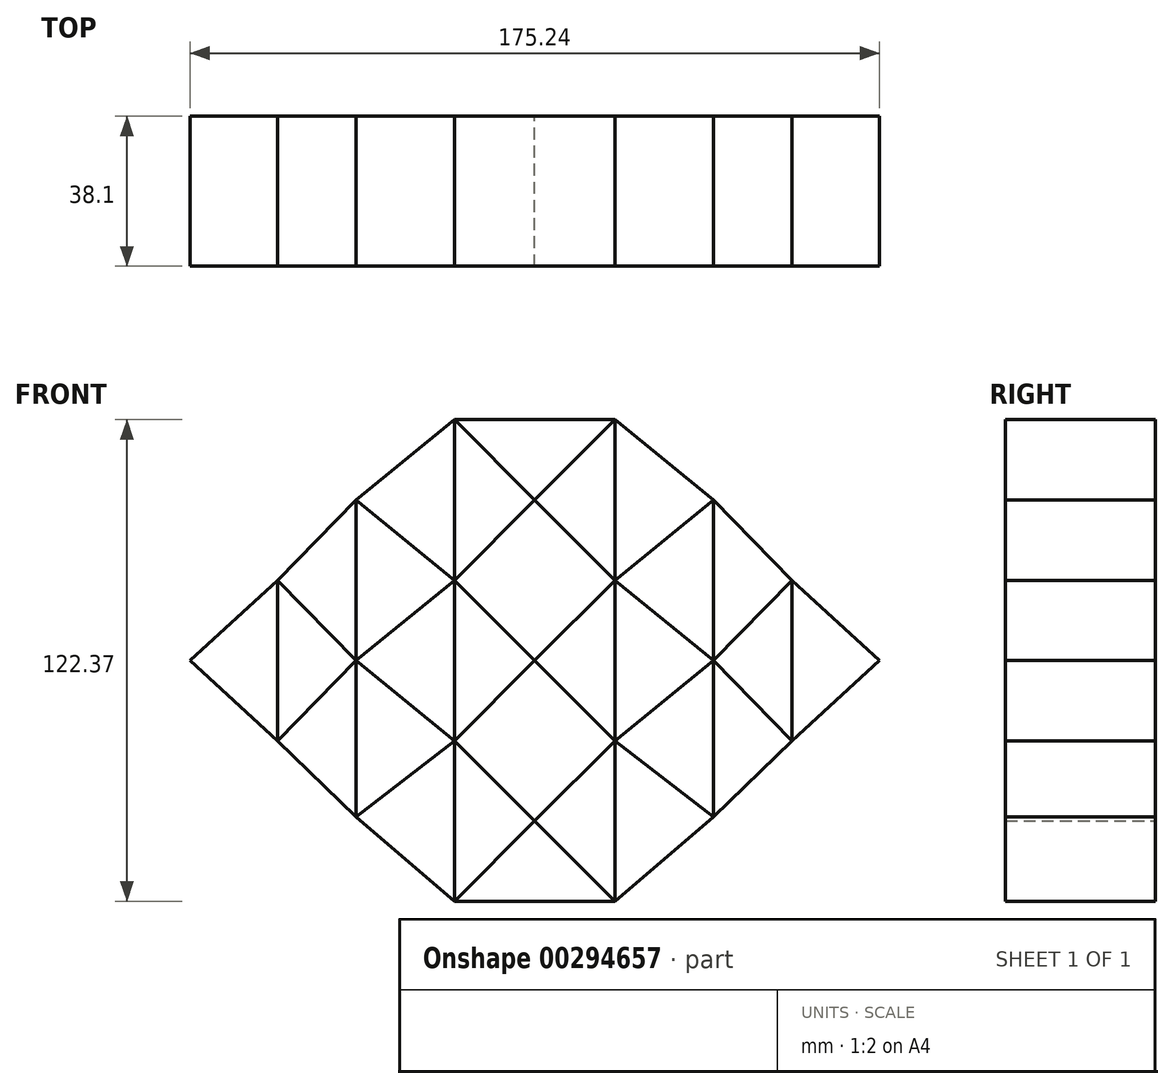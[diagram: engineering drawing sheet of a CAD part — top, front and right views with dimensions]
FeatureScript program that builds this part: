
annotation { "Feature Type Name" : "Feature", "Feature Type Description" : "" }
export const myFeature = defineFeature(function(context is Context, id is Id, definition is map)
    precondition{}
    {
        {
            var Q0;
            Q0=qCreatedBy(makeId("Front.planeOp"),FACE);
            var sketch = newSketch(context, id + "F0", { "sketchPlane" : qUnion([Q0])});
            skLineSegment(sketch, "E0", {"start": v(-20.4, 76.52) * mm, "end": v(16.8, 39.33) * mm});
            skLineSegment(sketch, "E1.MirrorCS", {"start": v(20.4, 76.52) * mm, "end": v(0, 56.12) * mm});
            skLineSegment(sketch, "E2.MirrorCS", {"start": v(-20.4, 35.73) * mm, "end": v(0, 56.12) * mm});
            skLineSegment(sketch, "E3.MirrorCS", {"start": v(16.8, 39.33) * mm, "end": v(-3.6, 59.72) * mm});
            skLineSegment(sketch, "E4.MirrorCS", {"start": v(-20.4, 35.73) * mm, "end": v(15.33, 0) * mm});
            skLineSegment(sketch, "E5.MirrorCS", {"start": v(20.4, 35.73) * mm, "end": v(0, 15.33) * mm});
            skLineSegment(sketch, "E6.MirrorCS", {"start": v(-20.4, -5.06) * mm, "end": v(0, 15.33) * mm});
            skLineSegment(sketch, "E7.MirrorCS", {"start": v(20.4, -5.06) * mm, "end": v(0, 15.33) * mm});
            skPoint(sketch, "E8.end.orphan", {"position": v(0, 0) * mm});
            skPoint(sketch, "E8.start.orphan", {"position": v(-20.4, 35.73) * mm});
            skPoint(sketch, "E9.start.orphan", {"position": v(16.8, 39.33) * mm});
            skLineSegment(sketch, "E10.MirrorCS", {"start": v(-20.4, -5.06) * mm, "end": v(0, -25.46) * mm});
            skLineSegment(sketch, "E11.MirrorCS", {"start": v(20.4, -5.06) * mm, "end": v(0, -25.46) * mm});
            skLineSegment(sketch, "E12.MirrorCS", {"start": v(-20.4, -45.85) * mm, "end": v(0, -25.46) * mm});
            skLineSegment(sketch, "E13.MirrorCS", {"start": v(20.4, -45.85) * mm, "end": v(0, -25.46) * mm});
            skPoint(sketch, "E14.orphan", {"position": v(0, 76.52) * mm});
            skLineSegment(sketch, "E15", {"start": v(-20.4, 76.52) * mm, "end": v(-20.4, -45.85) * mm});
            skLineSegment(sketch, "E16", {"start": v(20.4, -45.85) * mm, "end": v(20.4, 76.52) * mm});
            skLineSegment(sketch, "E17", {"start": v(20.4, 76.52) * mm, "end": v(-20.4, 76.52) * mm});
            skLineSegment(sketch, "E18", {"start": v(-20.4, -45.85) * mm, "end": v(20.4, -45.85) * mm});
            skLineSegment(sketch, "E19", {"start": v(16.8, 39.33) * mm, "end": v(20.4, 35.73) * mm});
            skPoint(sketch, "E20.start.orphan", {"position": v(20.4, 16.97) * mm});
            skPoint(sketch, "E21.endSnap0", {"position": v(20.4, 15.33) * mm});
            skLineSegment(sketch, "E22", {"start": v(45.38, 56.12) * mm, "end": v(20.4, 76.52) * mm});
            skLineSegment(sketch, "E23", {"start": v(45.38, 56.12) * mm, "end": v(20.4, 35.73) * mm});
            skLineSegment(sketch, "E24", {"start": v(20.4, 35.73) * mm, "end": v(45.38, 15.33) * mm});
            skLineSegment(sketch, "E25", {"start": v(45.38, 15.33) * mm, "end": v(20.4, -5.06) * mm});
            skLineSegment(sketch, "E26", {"start": v(20.4, -5.06) * mm, "end": v(45.38, -24.44) * mm});
            skLineSegment(sketch, "E27", {"start": v(45.38, -24.44) * mm, "end": v(20.4, -45.85) * mm});
            skLineSegment(sketch, "E28.MirrorCS", {"start": v(-45.38, 56.12) * mm, "end": v(-20.4, 76.52) * mm});
            skLineSegment(sketch, "E29.MirrorCS", {"start": v(-45.38, 56.12) * mm, "end": v(-20.4, 35.73) * mm});
            skLineSegment(sketch, "E30.MirrorCS", {"start": v(-20.4, 35.73) * mm, "end": v(-45.38, 15.33) * mm});
            skLineSegment(sketch, "E31.MirrorCS", {"start": v(-45.38, 15.33) * mm, "end": v(-20.4, -5.06) * mm});
            skLineSegment(sketch, "E32.MirrorCS", {"start": v(-20.4, -5.06) * mm, "end": v(-45.38, -24.44) * mm});
            skLineSegment(sketch, "E33.MirrorCS", {"start": v(-45.38, -24.44) * mm, "end": v(-20.4, -45.85) * mm});
            skLineSegment(sketch, "E34", {"start": v(-45.38, 56.12) * mm, "end": v(-45.38, -24.44) * mm});
            skLineSegment(sketch, "E35", {"start": v(45.38, -24.44) * mm, "end": v(45.38, 56.12) * mm});
            skLineSegment(sketch, "E36", {"start": v(45.38, 56.12) * mm, "end": v(65.28, 35.73) * mm});
            skLineSegment(sketch, "E37", {"start": v(65.28, 35.73) * mm, "end": v(45.38, 15.33) * mm});
            skLineSegment(sketch, "E38", {"start": v(65.28, -5.06) * mm, "end": v(45.38, 15.33) * mm});
            skLineSegment(sketch, "E39", {"start": v(65.28, -5.06) * mm, "end": v(45.38, -24.44) * mm});
            skLineSegment(sketch, "E40", {"start": v(65.28, 35.73) * mm, "end": v(65.28, -5.06) * mm});
            skPoint(sketch, "E41.endSnap0", {"position": v(65.28, 15.33) * mm});
            skLineSegment(sketch, "E42", {"start": v(87.62, 15.33) * mm, "end": v(65.28, 35.73) * mm});
            skLineSegment(sketch, "E43", {"start": v(87.62, 15.33) * mm, "end": v(65.28, -5.06) * mm});
            skLineSegment(sketch, "E44.MirrorCS", {"start": v(-45.38, 56.12) * mm, "end": v(-65.28, 35.73) * mm});
            skLineSegment(sketch, "E45.MirrorCS", {"start": v(-65.28, 35.73) * mm, "end": v(-65.28, -5.06) * mm});
            skLineSegment(sketch, "E46.MirrorCS", {"start": v(-65.28, 35.73) * mm, "end": v(-45.38, 15.33) * mm});
            skLineSegment(sketch, "E47.MirrorCS", {"start": v(-65.28, -5.06) * mm, "end": v(-45.38, 15.33) * mm});
            skLineSegment(sketch, "E48.MirrorCS", {"start": v(-65.28, -5.06) * mm, "end": v(-45.38, -24.44) * mm});
            skLineSegment(sketch, "E49.MirrorCS", {"start": v(-87.62, 15.33) * mm, "end": v(-65.28, -5.06) * mm});
            skLineSegment(sketch, "E50.MirrorCS", {"start": v(-87.62, 15.33) * mm, "end": v(-65.28, 35.73) * mm});
            skPoint(sketch, "E51.trimOffspring.end.orphan", {"position": v(0, -45.85) * mm});
            skSolve(sketch);
        }
        {
            var Q0;
            Q0=makeQuery(id+"F0.imprint","IMPRINT",FACE,{"disambiguationData":[TD([[makeQuery(id+"F0.imprint","IMPRINT",EDGE,{"derivedFrom":sQuery(id+"F0.wireOp",EDGE,"E45.MirrorCS")}),-1.0]])]});
            var Q1;
            {var subQ0=sQuery(id+"F0.wireOp",EDGE,"E44.MirrorCS");Q1=makeQuery(id+"F0.imprint","IMPRINT",FACE,{"disambiguationData":[TD([[makeQuery(id+"F0.imprint","IMPRINT",EDGE,{"derivedFrom":subQ0}),1.0]])]});}
            var Q2;
            {var subQ0=sQuery(id+"F0.wireOp",EDGE,"E47.MirrorCS");Q2=makeQuery(id+"F0.imprint","IMPRINT",FACE,{"disambiguationData":[TD([[makeQuery(id+"F0.imprint","IMPRINT",EDGE,{"derivedFrom":subQ0}),-1.0]])]});}
            var Q3;
            {var subQ0=sQuery(id+"F0.wireOp",EDGE,"E32.MirrorCS");Q3=makeQuery(id+"F0.imprint","IMPRINT",FACE,{"disambiguationData":[TD([[makeQuery(id+"F0.imprint","IMPRINT",EDGE,{"derivedFrom":subQ0}),1.0]])]});}
            var Q4;
            {var subQ0=sQuery(id+"F0.wireOp",EDGE,"E30.MirrorCS");Q4=makeQuery(id+"F0.imprint","IMPRINT",FACE,{"disambiguationData":[TD([[makeQuery(id+"F0.imprint","IMPRINT",EDGE,{"derivedFrom":subQ0}),1.0]])]});}
            var Q5;
            {var subQ0=sQuery(id+"F0.wireOp",EDGE,"E28.MirrorCS");Q5=makeQuery(id+"F0.imprint","IMPRINT",FACE,{"disambiguationData":[TD([[makeQuery(id+"F0.imprint","IMPRINT",EDGE,{"derivedFrom":subQ0}),-1.0]])]});}
            var Q6;
            {var subQ0=sQuery(id+"F0.wireOp",EDGE,"E0");Q6=makeQuery(id+"F0.imprint","IMPRINT",FACE,{"disambiguationData":[TD([[makeQuery(id+"F0.imprint","IMPRINT",EDGE,{"derivedFrom":subQ0}),1.0]])]});}
            var Q7;
            {var subQ1=sQuery(id+"F0.wireOp",EDGE,"E2.MirrorCS");Q7=makeQuery(id+"F0.imprint","IMPRINT",FACE,{"disambiguationData":[TD([[makeQuery(id+"F0.imprint","IMPRINT",EDGE,{"derivedFrom":subQ1}),-1.0]])]});}
            var Q8;
            {var subQ1=sQuery(id+"F0.wireOp",EDGE,"E6.MirrorCS");Q8=makeQuery(id+"F0.imprint","IMPRINT",FACE,{"disambiguationData":[TD([[makeQuery(id+"F0.imprint","IMPRINT",EDGE,{"derivedFrom":subQ1}),-1.0]])]});}
            var Q9;
            Q9=makeQuery(id+"F0.imprint","IMPRINT",FACE,{"disambiguationData":[TD([[makeQuery(id+"F0.imprint","IMPRINT",EDGE,{"derivedFrom":sQuery(id+"F0.wireOp",EDGE,"E12.MirrorCS")}),-1.0]])]});
            var Q10;
            {var subQ0=sQuery(id+"F0.wireOp",EDGE,"E26");Q10=makeQuery(id+"F0.imprint","IMPRINT",FACE,{"disambiguationData":[TD([[makeQuery(id+"F0.imprint","IMPRINT",EDGE,{"derivedFrom":subQ0}),-1.0]])]});}
            var Q11;
            {var subQ0=sQuery(id+"F0.wireOp",EDGE,"E24");Q11=makeQuery(id+"F0.imprint","IMPRINT",FACE,{"disambiguationData":[TD([[makeQuery(id+"F0.imprint","IMPRINT",EDGE,{"derivedFrom":subQ0}),-1.0]])]});}
            var Q12;
            {var subQ0=sQuery(id+"F0.wireOp",EDGE,"E22");Q12=makeQuery(id+"F0.imprint","IMPRINT",FACE,{"disambiguationData":[TD([[makeQuery(id+"F0.imprint","IMPRINT",EDGE,{"derivedFrom":subQ0}),1.0]])]});}
            var Q13;
            {var subQ0=sQuery(id+"F0.wireOp",EDGE,"E36");Q13=makeQuery(id+"F0.imprint","IMPRINT",FACE,{"disambiguationData":[TD([[makeQuery(id+"F0.imprint","IMPRINT",EDGE,{"derivedFrom":subQ0}),-1.0]])]});}
            var Q14;
            {var subQ0=sQuery(id+"F0.wireOp",EDGE,"E38");Q14=makeQuery(id+"F0.imprint","IMPRINT",FACE,{"disambiguationData":[TD([[makeQuery(id+"F0.imprint","IMPRINT",EDGE,{"derivedFrom":subQ0}),1.0]])]});}
            var Q15;
            Q15=makeQuery(id+"F0.imprint","IMPRINT",FACE,{"disambiguationData":[TD([[makeQuery(id+"F0.imprint","IMPRINT",EDGE,{"derivedFrom":sQuery(id+"F0.wireOp",EDGE,"E40")}),1.0]])]});
            extrude(context, id + "F1", {"entities" : qUnion([Q0, Q1, Q2, Q3, Q4, Q5, Q6, Q7, Q8, Q9, Q10, Q11, Q12, Q13, Q14, Q15]), "depth" : 38.1 * mm});
        }
    });
